# Revit family: Bidet_Seat-Round_Closed_Front-KOHLER-Novita-K-BN330S_1
name_source: partatom
category: Plumbing Fixtures
units: mm (PartAtom-declared; Revit-internal decimal feet)

## family parameters
Cut with Voids When Loaded = No
Host = Face
OmniClass Number = 23.31.19.19.17
OmniClass Title = Water Closet Seats
Part Type = Normal
Room Calculation Point = No
Round Connector Dimension = Use Diameter
Shared = No

## types (1)
- N0-White
    ADA Compliant = No
    Apparent Load = 1800 VA
    Assembly Code = D2010
    CW Connection = Yes
    Cold Water Inlet = Cold Water Inlet
    Date Modified = 04/18/2023
    Default Elevation = 15"
    Description = Round-Front Bidet Toilet Seat
    Drain Included = No
    Electrical Connector = Yes
    Electrical Note = One dedicated circuit required, protected with Class A Ground-Fault Circuit-Interrupter (GFCI)
    Finish = Kohler-Plastic-N0-White
    Flow Rate = 0 GPM
    HW Connection = No
    Height = 5"
    Hot Water Inlet = Hot Water Inlet
    Length = 19 15/16"
    Manufacturer = Kohler Co.
    Master Format 2014 = 22 41 13.19
    Master Format 2014 Name = Residential Bidets
    Material = Plastic Construction
    Model = K-BN330S-N0
    Pressure = 0.00 psi
    Product Documentation Link = https://www.us.kohler.com
    Product Name = Novita
    Product Page URL = http://www.us.kohler.com
    Type = 1
    URL = https://www.us.kohler.com
    Vent Connection = No
    Voltage = 120 V
    Waste Connection = No
    Waste Water Outlet = Waste Water Outlet
    WaterSense Certified = No
    Width = 15 3/16"

## geometry (parser evidence)
native form markers: Sweep x5
no freeform markers — native parametric forms only
